FCSTD DOCUMENT  (FreeCAD 0.19R23578 (Git))
Label: z_axis_assembly
License: All rights reserved
LicenseURL: http://en.wikipedia.org/wiki/All_rights_reserved
objects: App::Link×12, App::DocumentObjectGroup×2, PartDesign::CoordinateSystem×2, App::FeaturePython×1, App::Part×1
note: 2 computed .brp shape members not serialized (recipe doc carries the construction recipe); baked Part::Feature solids carry a one-line shape summary decoded from their .brp
EXTERNAL_REF file=nut_block_t8_leadscrew.FCStd obj=LCS_1
EXTERNAL_REF file=nut_block_t8_leadscrew.FCStd obj=nut_block_t8_leadscrew
EXTERNAL_REF file=nut_block_standoff.FCStd obj=LCS_2
EXTERNAL_REF file=nut_block_t8_leadscrew.FCStd obj=LCS_0
EXTERNAL_REF file=nut_block_standoff.FCStd obj=Part018
EXTERNAL_REF file=nut_block_standoff.FCStd obj=LCS_1
EXTERNAL_REF file=z_axis_bearing_plate.FCStd obj=LCS_1
EXTERNAL_REF file=z_axis_bearing_plate.FCStd obj=Part017
EXTERNAL_REF file=SC12UU_bearing_block.FCStd obj=LCS_1
EXTERNAL_REF file=z_axis_bearing_plate.FCStd obj=LCS_2
EXTERNAL_REF file=SC12UU_bearing_block.FCStd obj=Part
EXTERNAL_REF file=z_axis_bearing_plate.FCStd obj=LCS_3
EXTERNAL_REF file=z_axis_bearing_plate.FCStd obj=LCS_4
EXTERNAL_REF file=z_axis_bearing_plate.FCStd obj=LCS_5
EXTERNAL_REF file=V-Slot 20x80x500 Linear Rail.FCStd obj=LCS_1
EXTERNAL_REF file=z_axis_bearing_plate.FCStd obj=LCS_6
EXTERNAL_REF file=V-Slot 20x80x500 Linear Rail.FCStd obj=Part
EXTERNAL_REF file=V-Slot 20x80x500 Linear Rail.FCStd obj=LCS_3
EXTERNAL_REF file=y_motor_bracket.FCStd obj=LCS_2
EXTERNAL_REF file=y_motor_bracket.FCStd obj=Part022
EXTERNAL_REF file=Nema 17  Stepper Motor length 60mm.FcStd obj=LCS_0
EXTERNAL_REF file=y_motor_bracket.FCStd obj=LCS_1
EXTERNAL_REF file=Nema 17  Stepper Motor length 60mm.FcStd obj=Part
EXTERNAL_REF file=Nema 17  Stepper Motor length 60mm.FcStd obj=LCS_1
EXTERNAL_REF file=2gt_pulley_20t.FCStd obj=LCS_1
EXTERNAL_REF file=2gt_pulley_20t.FCStd obj=Part
EXTERNAL_REF file=V-Slot 20x80x500 Linear Rail.FCStd obj=LCS_2
EXTERNAL_REF file=carriage_assembly.FCStd obj=LCS_1
EXTERNAL_REF file=carriage_assembly.FCStd obj=Model

FEATURE [App::DocumentObjectGroup] Parts
FEATURE [PartDesign::CoordinateSystem] LCS_Origin
  AttacherType = Attacher::AttachEngine3D
  MapMode = 2
  Support = -> [X_Axis]
FEATURE [App::DocumentObjectGroup] Constraints
FEATURE [App::FeaturePython] Variables  # WARN: FeaturePython — macro-defined, semantics opaque (R4)
FEATURE [App::Link] nut_block_t8_leadscrew_nut_block_t8_leadscrew
  AssemblyType = Asm4EE
  AttachedBy = #LCS_1
  AttachedTo = Parent Assembly#LCS_Origin
  AttachmentOffset = pos=(0,0,0) rot=(-1,0,0;4.71239rad)
  LinkPlacement = pos=(7.3e-15,5.3e-15,-10) rot=(0,0,1;4.71239rad)
  LinkedObject = -> <external nut_block_t8_leadscrew.FCStd>#nut_block_t8_leadscrew
  Placement = pos=(7.3e-15,5.3e-15,-10) rot=(0,0,1;4.71239rad)
  expr: Placement = LCS_Origin.Placement * AttachmentOffset * nut_block_t8_leadscrew#LCS_1.Placement ^ -1
FEATURE [App::Link] nut_block_standoff_nut_block_standoff
  AssemblyType = Asm4EE
  AttachedBy = #LCS_2
  AttachedTo = nut_block_t8_leadscrew_nut_block_t8_leadscrew#LCS_0
  AttachmentOffset = pos=(0,0,0) rot=(0,1,0;3.14159rad)
  LinkPlacement = pos=(28.4,6.44136e-07,6.5) rot=(-0.57735,-0.57735,0.57735;2.0944rad)
  LinkedObject = -> <external nut_block_standoff.FCStd>#Part018
  Placement = pos=(28.4,6.44136e-07,6.5) rot=(-0.57735,-0.57735,0.57735;2.0944rad)
  expr: Placement = nut_block_t8_leadscrew_nut_block_t8_leadscrew.Placement * nut_block_t8_leadscrew#LCS_0.Placement * AttachmentOffset * nut_block_standoff#LCS_2.Placement ^ -1
FEATURE [App::Link] z_axis_bearing_plate_bearing_plate
  AssemblyType = Asm4EE
  AttachedBy = #LCS_1
  AttachedTo = nut_block_standoff_nut_block_standoff#LCS_1
  AttachmentOffset = pos=(0,0,0) rot=(0,0,1;1.5708rad)
  LinkPlacement = pos=(28.4,6.44136e-07,6.5) rot=(0.57735,0.57735,0.57735;2.0944rad)
  LinkedObject = -> <external z_axis_bearing_plate.FCStd>#Part017
  Placement = pos=(28.4,6.44136e-07,6.5) rot=(0.57735,0.57735,0.57735;2.0944rad)
  expr: Placement = nut_block_standoff_nut_block_standoff.Placement * nut_block_standoff#LCS_1.Placement * AttachmentOffset * z_axis_bearing_plate#LCS_1.Placement ^ -1
FEATURE [App::Link] SC12UU_bearing_block_SC12UU_bearing_block
  AssemblyType = Asm4EE
  AttachedBy = #LCS_1
  AttachedTo = z_axis_bearing_plate_bearing_plate#LCS_2
  LinkPlacement = pos=(28.4,-95.25,-14.5) rot=(0,0,1;4.71239rad)
  LinkedObject = -> <external SC12UU_bearing_block.FCStd>#Part
  Placement = pos=(28.4,-95.25,-14.5) rot=(0,0,1;4.71239rad)
  expr: Placement = z_axis_bearing_plate_bearing_plate.Placement * z_axis_bearing_plate#LCS_2.Placement * AttachmentOffset * SC12UU_bearing_block#LCS_1.Placement ^ -1
FEATURE [App::Link] SC12UU_bearing_block_SC12UU_bearing_block_2
  AssemblyType = Asm4EE
  AttachedBy = #LCS_1
  AttachedTo = z_axis_bearing_plate_bearing_plate#LCS_3
  LinkPlacement = pos=(28.4,-95.25,27.5) rot=(0,0,1;4.71239rad)
  LinkedObject = -> <external SC12UU_bearing_block.FCStd>#Part
  Placement = pos=(28.4,-95.25,27.5) rot=(0,0,1;4.71239rad)
  expr: Placement = z_axis_bearing_plate_bearing_plate.Placement * z_axis_bearing_plate#LCS_3.Placement * AttachmentOffset * SC12UU_bearing_block#LCS_1.Placement ^ -1
FEATURE [App::Link] SC12UU_bearing_block_SC12UU_bearing_block_3
  AssemblyType = Asm4EE
  AttachedBy = #LCS_1
  AttachedTo = z_axis_bearing_plate_bearing_plate#LCS_4
  LinkPlacement = pos=(28.4,95.25,-14.5) rot=(0,0,1;4.71239rad)
  LinkedObject = -> <external SC12UU_bearing_block.FCStd>#Part
  Placement = pos=(28.4,95.25,-14.5) rot=(0,0,1;4.71239rad)
  expr: Placement = z_axis_bearing_plate_bearing_plate.Placement * z_axis_bearing_plate#LCS_4.Placement * AttachmentOffset * SC12UU_bearing_block#LCS_1.Placement ^ -1
FEATURE [App::Link] SC12UU_bearing_block_SC12UU_bearing_block_4
  AssemblyType = Asm4EE
  AttachedBy = #LCS_1
  AttachedTo = z_axis_bearing_plate_bearing_plate#LCS_5
  LinkPlacement = pos=(28.4,95.25,27.5) rot=(0,0,1;4.71239rad)
  LinkedObject = -> <external SC12UU_bearing_block.FCStd>#Part
  Placement = pos=(28.4,95.25,27.5) rot=(0,0,1;4.71239rad)
  expr: Placement = z_axis_bearing_plate_bearing_plate.Placement * z_axis_bearing_plate#LCS_5.Placement * AttachmentOffset * SC12UU_bearing_block#LCS_1.Placement ^ -1
FEATURE [App::Link] V_Slot_20x80x500_Linear_Rail_V_Slot_20x80x500_Linear_Rail  label="V_Slot_20x80x500_Linear_Rail_V-Slot 20x80x500 Linear Rail"
  AssemblyType = Asm4EE
  AttachedBy = #LCS_1
  AttachedTo = z_axis_bearing_plate_bearing_plate#LCS_6
  AttachmentOffset = pos=(0,0,0) rot=(0,0,1;1.5708rad)
  LinkPlacement = pos=(44.75,250,6.5) rot=(1,0,0;1.5708rad)
  LinkedObject = -> <external V-Slot 20x80x500 Linear Rail.FCStd>#Part
  Placement = pos=(44.75,250,6.5) rot=(1,0,0;1.5708rad)
  expr: Placement = z_axis_bearing_plate_bearing_plate.Placement * z_axis_bearing_plate#LCS_6.Placement * AttachmentOffset * V_Slot_20x80x500_Linear_Rail#LCS_1.Placement ^ -1
FEATURE [App::Link] y_motor_bracket_y_motor_bracket
  AssemblyType = Asm4EE
  AttachedBy = #LCS_2
  AttachedTo = V_Slot_20x80x500_Linear_Rail_V_Slot_20x80x500_Linear_Rail#LCS_3
  AttachmentOffset = pos=(0,0,0) rot=(0,0,1;4.71239rad)
  LinkPlacement = pos=(30.75,-252.5,18) rot=(0,0,1;0rad)
  LinkedObject = -> <external y_motor_bracket.FCStd>#Part022
  Placement = pos=(30.75,-252.5,18) rot=(0,0,1;0rad)
  expr: Placement = V_Slot_20x80x500_Linear_Rail_V_Slot_20x80x500_Linear_Rail.Placement * V_Slot_20x80x500_Linear_Rail#LCS_3.Placement * AttachmentOffset * y_motor_bracket#LCS_2.Placement ^ -1
FEATURE [App::Link] Nema_17__Stepper_Motor_length_60mm_Nema_17__Stepper_Motor_length_60mm  label="Nema_17__Stepper_Motor_length_60mm_Nema 17  Stepper Motor length 60mm"
  AssemblyType = Asm4EE
  AttachedBy = #LCS_0
  AttachedTo = y_motor_bracket_y_motor_bracket#LCS_1
  LinkPlacement = pos=(54.75,-274.5,81.4) rot=(-0.57735,0.57735,0.57735;4.18879rad)
  LinkedObject = -> <external Nema 17  Stepper Motor length 60mm.FcStd>#Part
  Placement = pos=(54.75,-274.5,81.4) rot=(-0.57735,0.57735,0.57735;4.18879rad)
  expr: Placement = y_motor_bracket_y_motor_bracket.Placement * y_motor_bracket#LCS_1.Placement * AttachmentOffset * Nema_17__Stepper_Motor_length_60mm#LCS_0.Placement ^ -1
FEATURE [App::Link] _gt_pulley_20t_2gt_pulley_20t
  AssemblyType = Asm4EE
  AttachedBy = #LCS_1
  AttachedTo = Nema_17__Stepper_Motor_length_60mm_Nema_17__Stepper_Motor_length_60mm#LCS_1
  AttachmentOffset = pos=(0,0,0) rot=(1,0,0;3.14159rad)
  LinkPlacement = pos=(54.75,-274.5,-2.2) rot=(0,-1,0;1.5708rad)
  LinkedObject = -> <external 2gt_pulley_20t.FCStd>#Part
  Placement = pos=(54.75,-274.5,-2.2) rot=(0,-1,0;1.5708rad)
  expr: Placement = Nema_17__Stepper_Motor_length_60mm_Nema_17__Stepper_Motor_length_60mm.Placement * Nema_17__Stepper_Motor_length_60mm#LCS_1.Placement * AttachmentOffset * _gt_pulley_20t#LCS_1.Placement ^ -1
FEATURE [App::Link] carriage_assembly
  AssemblyType = Asm4EE
  AttachedBy = #LCS_1
  AttachedTo = V_Slot_20x80x500_Linear_Rail_V_Slot_20x80x500_Linear_Rail#LCS_2
  LinkPlacement = pos=(56.25,1.2758e-06,6.5) rot=(0,0,1;0rad)
  LinkedObject = -> <external carriage_assembly.FCStd>#Model
  Placement = pos=(56.25,1.2758e-06,6.5) rot=(0,0,1;0rad)
  expr: Placement = V_Slot_20x80x500_Linear_Rail_V_Slot_20x80x500_Linear_Rail.Placement * V_Slot_20x80x500_Linear_Rail#LCS_2.Placement * AttachmentOffset * carriage_assembly#LCS_1.Placement ^ -1
FEATURE [PartDesign::CoordinateSystem] LCS_1
  AttacherType = Attacher::AttachEngine3D
  Placement = pos=(0,1e-15,2e-15) rot=(1,0,0;1.5708rad)
  expr: Placement = nut_block_t8_leadscrew_nut_block_t8_leadscrew.Placement * nut_block_t8_leadscrew#LCS_1.Placement * AttachmentOffset
FEATURE [App::Part] Model
  Configuration = 0
  Group = -> [LCS_Origin,Constraints,Variables,nut_block_t8_leadscrew_nut_block_t8_leadscrew,nut_block_standoff_nut_block_standoff,z_axis_bearing_plate_bearing_plate,SC12UU_bearing_block_SC12UU_bearing_block,SC12UU_bearing_block_SC12UU_bearing_block_2,SC12UU_bearing_block_SC12UU_bearing_block_3,SC12UU_bearing_block_SC12UU_bearing_block_4,V_Slot_20x80x500_Linear_Rail_V_Slot_20x80x500_Linear_Rail,+5 more]
  Origin = -> Origin
  Type = Assembly4 Model

RESOLVED EXTERNAL PARTS (link-assembly join: the EXTERNAL_REF files above that resolve inside this repo's crawl, each included once):
---- part carriage_assembly.FCStd = doc fcstd_ae16f4e09451 ----
FCSTD DOCUMENT  (FreeCAD 0.19R23578 (Git))
Label: carriage_assembly
License: All rights reserved
LicenseURL: http://en.wikipedia.org/wiki/All_rights_reserved
objects: App::Link×16, App::DocumentObjectGroup×2, PartDesign::CoordinateSystem×2, App::FeaturePython×1, App::Part×1
note: 2 computed .brp shape members not serialized (recipe doc carries the construction recipe); baked Part::Feature solids carry a one-line shape summary decoded from their .brp
EXTERNAL_REF file=y_axis_carriage_block.FCStd obj=Part026
EXTERNAL_REF file=x_axis_rail.FCStd obj=LCS_2
EXTERNAL_REF file=y_axis_carriage_block.FCStd obj=LCS_4
EXTERNAL_REF file=x_axis_rail.FCStd obj=Part028
EXTERNAL_REF file=x_axis_rail.FCStd obj=LCS_1
EXTERNAL_REF file=x_idler_bracket.FCStd obj=LCS_1
EXTERNAL_REF file=x_idler_bracket.FCStd obj=Part033
EXTERNAL_REF file=gates_2gt_idler_toothed.FCStd obj=LCS_1
EXTERNAL_REF file=x_idler_bracket.FCStd obj=LCS_2
EXTERNAL_REF file=gates_2gt_idler_toothed.FCStd obj=Part042
EXTERNAL_REF file=stock_motor_mount.FCStd obj=LCS_6
EXTERNAL_REF file=y_axis_carriage_block.FCStd obj=LCS_15
EXTERNAL_REF file=stock_motor_mount.FCStd obj=Part
EXTERNAL_REF file=Nema 17  Stepper Motor length 60mm.FcStd obj=LCS_0
EXTERNAL_REF file=stock_motor_mount.FCStd obj=LCS_1
EXTERNAL_REF file=Nema 17  Stepper Motor length 60mm.FcStd obj=Part
EXTERNAL_REF file=Nema 17  Stepper Motor length 60mm.FcStd obj=LCS_1
EXTERNAL_REF file=2gt_pulley_20t.FCStd obj=LCS_1
EXTERNAL_REF file=2gt_pulley_20t.FCStd obj=Part
EXTERNAL_REF file=watercooled_print_head.FCStd obj=LCS_1
EXTERNAL_REF file=x_axis_rail.FCStd obj=LCS_3
EXTERNAL_REF file=watercooled_print_head.FCStd obj=Model
EXTERNAL_REF file=Aluminum Spacer 6mm002.FCStd obj=LCS_1
EXTERNAL_REF file=y_axis_carriage_block.FCStd obj=LCS_12
EXTERNAL_REF file=Aluminum Spacer 6mm002.FCStd obj=Aluminum_Spacer_6mm002
EXTERNAL_REF file=y_axis_carriage_block.FCStd obj=LCS_11
EXTERNAL_REF file=eccentric_spacer.FCStd obj=LCS_1
EXTERNAL_REF file=y_axis_carriage_block.FCStd obj=LCS_13
EXTERNAL_REF file=eccentric_spacer.FCStd obj=Part
EXTERNAL_REF file=y_axis_carriage_block.FCStd obj=LCS_14
EXTERNAL_REF file=Aluminum Spacer 6mm002.FCStd obj=LCS_2
EXTERNAL_REF file=solid_v_wheel_assembly.FCStd obj=LCS_Origin
EXTERNAL_REF file=solid_v_wheel_assembly.FCStd obj=Model
EXTERNAL_REF file=eccentric_spacer.FCStd obj=LCS_2

FEATURE [App::DocumentObjectGroup] Parts
FEATURE [PartDesign::CoordinateSystem] LCS_Origin
  AttacherType = Attacher::AttachEngine3D
  MapMode = 2
  Support = -> [X_Axis]
FEATURE [App::DocumentObjectGroup] Constraints
FEATURE [App::FeaturePython] Variables  # WARN: FeaturePython — macro-defined, semantics opaque (R4)
FEATURE [App::Link] y_axis_carriage_block_y_axis_carriage_block001
  LinkedObject = -> <external y_axis_carriage_block.FCStd>#Part026
FEATURE [App::Link] x_axis_rail_2020_vslot_rail
  AssemblyType = Asm4EE
  AttachedBy = #LCS_2
  AttachedTo = y_axis_carriage_block_y_axis_carriage_block001#LCS_4
  AttachmentOffset = pos=(0,0,0) rot=(0,1,0;4.71239rad)
  LinkPlacement = pos=(57.675,-10,-1.34e-14) rot=(0.57735,-0.57735,0.57735;4.18879rad)
  LinkedObject = -> <external x_axis_rail.FCStd>#Part028
  Placement = pos=(57.675,-10,-1.34e-14) rot=(0.57735,-0.57735,0.57735;4.18879rad)
  expr: Placement = y_axis_carriage_block_y_axis_carriage_block001.Placement * y_axis_carriage_block#LCS_4.Placement * AttachmentOffset * x_axis_rail#LCS_2.Placement ^ -1
FEATURE [App::Link] x_idler_bracket_x_idler_bracket
  AssemblyType = Asm4EE
  AttachedBy = #LCS_1
  AttachedTo = x_axis_rail_2020_vslot_rail#LCS_1
  AttachmentOffset = pos=(0,0,0) rot=(0,0,1;4.71239rad)
  LinkPlacement = pos=(437.675,-10,-2.064e-13) rot=(0,0,1;0rad)
  LinkedObject = -> <external x_idler_bracket.FCStd>#Part033
  Placement = pos=(437.675,-10,-2.064e-13) rot=(0,0,1;0rad)
  expr: Placement = x_axis_rail_2020_vslot_rail.Placement * x_axis_rail#LCS_1.Placement * AttachmentOffset * x_idler_bracket#LCS_1.Placement ^ -1
FEATURE [App::Link] gates_2gt_idler_toothed_e3d_2gt_idler
  AssemblyType = Asm4EE
  AttachedBy = #LCS_1
  AttachedTo = x_idler_bracket_x_idler_bracket#LCS_2
  LinkPlacement = pos=(448.675,-24,-2.846e-13) rot=(-0.57735,-0.57735,-0.57735;2.0944rad)
  LinkedObject = -> <external gates_2gt_idler_toothed.FCStd>#Part042
  Placement = pos=(448.675,-24,-2.846e-13) rot=(-0.57735,-0.57735,-0.57735;2.0944rad)
  expr: Placement = x_idler_bracket_x_idler_bracket.Placement * x_idler_bracket#LCS_2.Placement * AttachmentOffset * gates_2gt_idler_toothed#LCS_1.Placement ^ -1
FEATURE [App::Link] stock_motor_mount_stock_motor_mount
  AssemblyType = Asm4EE
  AttachedBy = #LCS_6
  AttachedTo = y_axis_carriage_block_y_axis_carriage_block001#LCS_15
  LinkPlacement = pos=(9.35,-23,-36) rot=(0.57735,0.57735,0.57735;4.18879rad)
  LinkedObject = -> <external stock_motor_mount.FCStd>#Part
  Placement = pos=(9.35,-23,-36) rot=(0.57735,0.57735,0.57735;4.18879rad)
  expr: Placement = y_axis_carriage_block_y_axis_carriage_block001.Placement * y_axis_carriage_block#LCS_15.Placement * AttachmentOffset * stock_motor_mount#LCS_6.Placement ^ -1
FEATURE [App::Link] Nema_17__Stepper_Motor_length_60mm_Nema_17__Stepper_Motor_length_60mm  label="Nema_17__Stepper_Motor_length_60mm_Nema 17  Stepper Motor length 60mm"
  AssemblyType = Asm4EE
  AttachedBy = #LCS_0
  AttachedTo = stock_motor_mount_stock_motor_mount#LCS_1
  AttachmentOffset = pos=(0,0,0) rot=(1,0,0;3.14159rad)
  LinkPlacement = pos=(36.33,-23,73.42) rot=(0,0.707107,0.707107;3.14159rad)
  LinkedObject = -> <external Nema 17  Stepper Motor length 60mm.FcStd>#Part
  Placement = pos=(36.33,-23,73.42) rot=(0,0.707107,0.707107;3.14159rad)
  expr: Placement = stock_motor_mount_stock_motor_mount.Placement * stock_motor_mount#LCS_1.Placement * AttachmentOffset * Nema_17__Stepper_Motor_length_60mm#LCS_0.Placement ^ -1
FEATURE [App::Link] _gt_pulley_20t_2gt_pulley_20t
  AssemblyType = Asm4EE
  AttachedBy = #LCS_1
  AttachedTo = Nema_17__Stepper_Motor_length_60mm_Nema_17__Stepper_Motor_length_60mm#LCS_1
  AttachmentOffset = pos=(0,0,0) rot=(1,0,0;3.14159rad)
  LinkPlacement = pos=(36.33,-23,-10.18) rot=(-0.57735,-0.57735,-0.57735;2.0944rad)
  LinkedObject = -> <external 2gt_pulley_20t.FCStd>#Part
  Placement = pos=(36.33,-23,-10.18) rot=(-0.57735,-0.57735,-0.57735;2.0944rad)
  expr: Placement = Nema_17__Stepper_Motor_length_60mm_Nema_17__Stepper_Motor_length_60mm.Placement * Nema_17__Stepper_Motor_length_60mm#LCS_1.Placement * AttachmentOffset * _gt_pulley_20t#LCS_1.Placement ^ -1
FEATURE [App::Link] watercooled_print_head
  AssemblyType = Asm4EE
  AttachedBy = #LCS_1
  AttachedTo = x_axis_rail_2020_vslot_rail#LCS_3
  AttachmentOffset = pos=(0,0,0) rot=(0.57735,-0.57735,0.57735;2.0944rad)
  LinkPlacement = pos=(241.675,-40,-25) rot=(0,0,1;0rad)
  LinkedObject = -> <external watercooled_print_head.FCStd>#Model
  Placement = pos=(241.675,-40,-25) rot=(0,0,1;0rad)
  expr: Placement = x_axis_rail_2020_vslot_rail.Placement * x_axis_rail#LCS_3.Placement * AttachmentOffset * watercooled_print_head#LCS_1.Placement ^ -1
FEATURE [App::Link] Aluminum_Spacer_6mm002_Aluminum_Spacer_6mm002
  AssemblyType = Asm4EE
  AttachedBy = #LCS_1
  AttachedTo = y_axis_carriage_block_y_axis_carriage_block001#LCS_12
  LinkPlacement = pos=(-6,40,49.85) rot=(0,-1,0;4.71239rad)
  LinkedObject = -> <external Aluminum Spacer 6mm002.FCStd>#Aluminum_Spacer_6mm002
  Placement = pos=(-6,40,49.85) rot=(0,-1,0;4.71239rad)
  expr: Placement = y_axis_carriage_block_y_axis_carriage_block001.Placement * y_axis_carriage_block#LCS_12.Placement * AttachmentOffset * Aluminum_Spacer_6mm002#LCS_1.Placement ^ -1
FEATURE [App::Link] Aluminum_Spacer_6mm002_Aluminum_Spacer_6mm003
  AssemblyType = Asm4EE
  AttachedBy = #LCS_1
  AttachedTo = y_axis_carriage_block_y_axis_carriage_block001#LCS_11
  LinkPlacement = pos=(-6,-40,49.85) rot=(0,-1,0;4.71239rad)
  LinkedObject = -> <external Aluminum Spacer 6mm002.FCStd>#Aluminum_Spacer_6mm002
  Placement = pos=(-6,-40,49.85) rot=(0,-1,0;4.71239rad)
  expr: Placement = y_axis_carriage_block_y_axis_carriage_block001.Placement * y_axis_carriage_block#LCS_11.Placement * AttachmentOffset * Aluminum_Spacer_6mm002#LCS_1.Placement ^ -1
FEATURE [App::Link] eccentric_spacer_eccentric_spacer
  AssemblyType = Asm4EE
  AttachedBy = #LCS_1
  AttachedTo = y_axis_carriage_block_y_axis_carriage_block001#LCS_13
  AttachmentOffset = pos=(0,0,0) rot=(1,0,0;3.14159rad)
  LinkPlacement = pos=(0,40,-49.85) rot=(-0.707107,0,0.707107;3.14159rad)
  LinkedObject = -> <external eccentric_spacer.FCStd>#Part
  Placement = pos=(0,40,-49.85) rot=(-0.707107,0,0.707107;3.14159rad)
  expr: Placement = y_axis_carriage_block_y_axis_carriage_block001.Placement * y_axis_carriage_block#LCS_13.Placement * AttachmentOffset * eccentric_spacer#LCS_1.Placement ^ -1
FEATURE [App::Link] eccentric_spacer_eccentric_spacer_2
  AssemblyType = Asm4EE
  AttachedBy = #LCS_1
  AttachedTo = y_axis_carriage_block_y_axis_carriage_block001#LCS_14
  AttachmentOffset = pos=(0,0,0) rot=(0,-1,0;3.14159rad)
  LinkPlacement = pos=(0,-40,-49.85) rot=(0,-1,0;1.5708rad)
  LinkedObject = -> <external eccentric_spacer.FCStd>#Part
  Placement = pos=(0,-40,-49.85) rot=(0,-1,0;1.5708rad)
  expr: Placement = y_axis_carriage_block_y_axis_carriage_block001.Placement * y_axis_carriage_block#LCS_14.Placement * AttachmentOffset * eccentric_spacer#LCS_1.Placement ^ -1
FEATURE [App::Link] solid_v_wheel_assembly
  AssemblyType = Asm4EE
  AttachedBy = #LCS_Origin
  AttachedTo = Aluminum_Spacer_6mm002_Aluminum_Spacer_6mm002#LCS_2
  LinkPlacement = pos=(-6,40,49.85) rot=(0.57735,-0.57735,0.57735;4.18879rad)
  LinkedObject = -> <external solid_v_wheel_assembly.FCStd>#Model
  Placement = pos=(-6,40,49.85) rot=(0.57735,-0.57735,0.57735;4.18879rad)
  expr: Placement = Aluminum_Spacer_6mm002_Aluminum_Spacer_6mm002.Placement * Aluminum_Spacer_6mm002#LCS_2.Placement * AttachmentOffset * solid_v_wheel_assembly#LCS_Origin.Placement ^ -1
FEATURE [App::Link] solid_v_wheel_assembly_2
  AssemblyType = Asm4EE
  AttachedBy = #LCS_Origin
  AttachedTo = Aluminum_Spacer_6mm002_Aluminum_Spacer_6mm003#LCS_2
  LinkPlacement = pos=(-6,-40,49.85) rot=(0.57735,-0.57735,0.57735;4.18879rad)
  LinkedObject = -> <external solid_v_wheel_assembly.FCStd>#Model
  Placement = pos=(-6,-40,49.85) rot=(0.57735,-0.57735,0.57735;4.18879rad)
  expr: Placement = Aluminum_Spacer_6mm002_Aluminum_Spacer_6mm003.Placement * Aluminum_Spacer_6mm002#LCS_2.Placement * AttachmentOffset * solid_v_wheel_assembly#LCS_Origin.Placement ^ -1
FEATURE [App::Link] solid_v_wheel_assembly_3
  AssemblyType = Asm4EE
  AttachedBy = #LCS_Origin
  AttachedTo = eccentric_spacer_eccentric_spacer#LCS_2
  AttachmentOffset = pos=(0,0,0) rot=(0,-1,0;3.14159rad)
  LinkPlacement = pos=(-6,40.78,-49.85) rot=(0.57735,0.57735,0.57735;2.0944rad)
  LinkedObject = -> <external solid_v_wheel_assembly.FCStd>#Model
  Placement = pos=(-6,40.78,-49.85) rot=(0.57735,0.57735,0.57735;2.0944rad)
  expr: Placement = eccentric_spacer_eccentric_spacer.Placement * eccentric_spacer#LCS_2.Placement * AttachmentOffset * solid_v_wheel_assembly#LCS_Origin.Placement ^ -1
FEATURE [App::Link] solid_v_wheel_assembly_4
  AssemblyType = Asm4EE
  AttachedBy = #LCS_Origin
  AttachedTo = eccentric_spacer_eccentric_spacer_2#LCS_2
  AttachmentOffset = pos=(0,0,0) rot=(0,1,0;3.14159rad)
  LinkPlacement = pos=(-6,-40.78,-49.85) rot=(-0.57735,0.57735,-0.57735;2.0944rad)
  LinkedObject = -> <external solid_v_wheel_assembly.FCStd>#Model
  Placement = pos=(-6,-40.78,-49.85) rot=(-0.57735,0.57735,-0.57735;2.0944rad)
  expr: Placement = eccentric_spacer_eccentric_spacer_2.Placement * eccentric_spacer#LCS_2.Placement * AttachmentOffset * solid_v_wheel_assembly#LCS_Origin.Placement ^ -1
FEATURE [PartDesign::CoordinateSystem] LCS_1
  AttacherType = Attacher::AttachEngine3D
  AttachmentOffset = pos=(-11.5,0,0) rot=(0,0,1;0rad)
  MapMode = 2
  Placement = pos=(-11.5,0,0) rot=(0,0,1;0rad)
  Support = -> [LCS_Origin]
FEATURE [App::Part] Model
  Configuration = 0
  Group = -> [LCS_Origin,Constraints,Variables,y_axis_carriage_block_y_axis_carriage_block001,x_axis_rail_2020_vslot_rail,x_idler_bracket_x_idler_bracket,gates_2gt_idler_toothed_e3d_2gt_idler,stock_motor_mount_stock_motor_mount,Nema_17__Stepper_Motor_length_60mm_Nema_17__Stepper_Motor_length_60mm,_gt_pulley_20t_2gt_pulley_20t,watercooled_print_head,Aluminum_Spacer_6mm002_Aluminum_Spacer_6mm002,+8 more]
  Origin = -> Origin
  Type = Assembly4 Model
---- part nut_block_standoff.FCStd = doc fcstd_659b3a1c4ef2 ----
FCSTD DOCUMENT  (FreeCAD 0.19R23578 (Git))
Label: nut_block_standoff
License: All rights reserved
LicenseURL: http://en.wikipedia.org/wiki/All_rights_reserved
objects: Sketcher::SketchObject×3, PartDesign::Hole×2, PartDesign::CoordinateSystem×2, PartDesign::Pad×1, PartDesign::Body×1, App::Part×1
note: 12 computed .brp shape members not serialized (recipe doc carries the construction recipe); baked Part::Feature solids carry a one-line shape summary decoded from their .brp

FEATURE [Sketcher::SketchObject] Sketch026
  MapMode = 5
  Placement = pos=(0,0,0) rot=(0.57735,0.57735,0.57735;2.0944rad)
  Support = -> [YZ_Plane030]
  sketch-geometry (10):
    g0: LineSegment StartX=-30 StartY=0 StartZ=0 EndX=-30 EndY=2 EndZ=0
    g1: LineSegment StartX=-30 StartY=2 StartZ=0 EndX=-16.5 EndY=22.4 EndZ=0
    g2: LineSegment StartX=-16.5 StartY=22.4 StartZ=0 EndX=16.5 EndY=22.4 EndZ=0
    g3: LineSegment StartX=16.5 StartY=22.4 StartZ=0 EndX=30 EndY=2 EndZ=0
    g4: LineSegment StartX=30 StartY=2 StartZ=0 EndX=30 EndY=0 EndZ=0
    g5: LineSegment StartX=30 StartY=0 StartZ=0 EndX=-30 EndY=0 EndZ=0
    g6: ArcOfCircle CenterX=-11 CenterY=11.2 CenterZ=0 NormalX=0 NormalY=0 NormalZ=1 AngleXU=0 Radius=6.5 StartAngle=1.5708 EndAngle=4.71239
    g7: ArcOfCircle CenterX=11 CenterY=11.2 CenterZ=0 NormalX=0 NormalY=0 NormalZ=1 AngleXU=0 Radius=6.5 StartAngle=4.71239 EndAngle=7.85398
    g8: LineSegment StartX=-11 StartY=4.7 StartZ=0 EndX=11 EndY=4.7 EndZ=0
    g9: LineSegment StartX=-11 StartY=17.7 StartZ=0 EndX=11 EndY=17.7 EndZ=0
  constraints (25):
    c: Coincident(g0,g5)
    c: Coincident(g0,g1)
    c: Coincident(g1,g2)
    c: Coincident(g2,g3)
    c: Coincident(g3,g4)
    c: Coincident(g4,g5)
    c: Vertical(g0)
    c: Vertical(g4)
    c: PointOnObject(g-1,g5)
    c: DistanceX(g5,g5) = 60
    c: DistanceX(g2,g2) = 33
    c: DistanceY(g0,g0) = 2
    c: Equal(g0,g4)
    c: DistanceY(g4,g2) = 22.4
    c: Symmetric(g1,g2,g-2)
    c: Symmetric(g0,g4,g-2)
    c: Tangent(g6,g9) = 1.5708
    c: Tangent(g6,g8) = -1.5708
    c: Tangent(g8,g7) = -1.5708
    c: Tangent(g9,g7) = 1.5708
    c: Horizontal(g8)
    c: Symmetric(g6,g7,g-2)
    c: Distance(g6,g6) = 13
    c: DistanceY(g-1,g6) = 11.2
    c: DistanceX(g6,g7) = 22
FEATURE [PartDesign::Pad] Pad002
  AllowMultiFace = false
  Direction = (1,1,1)
  Length = 34
  Length2 = 100
  Midplane = true
  Placement = pos=(0,0,0) rot=(0.57735,0.57735,0.57735;2.0944rad)
  Profile = -> Sketch026
  Type = 0
FEATURE [Sketcher::SketchObject] Sketch027
  MapMode = 5
  Placement = pos=(0,0,0) rot=(0,1,0;3.14159rad)
  Support = -> [XY_Plane030]
  sketch-geometry (11):
    g0: Circle CenterX=-10 CenterY=24 CenterZ=0 NormalX=0 NormalY=0 NormalZ=1 AngleXU=0 Radius=2.5
    g1: Circle CenterX=-10 CenterY=-24 CenterZ=0 NormalX=0 NormalY=0 NormalZ=1 AngleXU=0 Radius=2.5
    g2: Circle CenterX=10 CenterY=-24 CenterZ=0 NormalX=0 NormalY=0 NormalZ=1 AngleXU=0 Radius=2.5
    g3: Circle CenterX=10 CenterY=24 CenterZ=0 NormalX=0 NormalY=0 NormalZ=1 AngleXU=0 Radius=2.5
    g4: LineSegment StartX=-10 StartY=24 StartZ=0 EndX=10 EndY=24 EndZ=0
    g5: LineSegment StartX=10 StartY=24 StartZ=0 EndX=10 EndY=-24 EndZ=0
    g6: LineSegment StartX=10 StartY=-24 StartZ=0 EndX=-10 EndY=-24 EndZ=0
    g7: LineSegment StartX=-10 StartY=-24 StartZ=0 EndX=-10 EndY=24 EndZ=0
    g8: LineSegment StartX=-10 StartY=24 StartZ=0 EndX=10 EndY=-24 EndZ=0
    g9: LineSegment StartX=-10 StartY=-24 StartZ=0 EndX=10 EndY=24 EndZ=0
    g10: GeomPoint X=0 Y=0 Z=0
  constraints (25):
    c: Coincident(g4,g5)
    c: Coincident(g5,g6)
    c: Coincident(g6,g7)
    c: Coincident(g7,g4)
    c: Horizontal(g4)
    c: Horizontal(g6)
    c: Vertical(g5)
    c: Vertical(g7)
    c: Coincident(g4,g0)
    c: Coincident(g5,g2)
    c: Coincident(g3,g4)
    c: Coincident(g1,g6)
    c: Diameter(g0) = 5
    c: Equal(g0,g3)
    c: Equal(g3,g1)
    c: Equal(g1,g2)
    c: Coincident(g8,g2)
    c: Coincident(g9,g1)
    c: Coincident(g9,g3)
    c: PointOnObject(g10,g8)
    c: PointOnObject(g10,g9)
    c: Coincident(g10,g-1)
    c: DistanceX(g6,g6) = 20
    c: Coincident(g8,g0)
    c: DistanceY(g5,g5) = 48
FEATURE [PartDesign::Hole] Hole002
  AllowMultiFace = false
  BaseFeature = -> Pad002
  Depth = 25
  DepthType = 1
  Diameter = 1.6
  DrillPoint = 0
  DrillPointAngle = 118
  HoleCutCountersinkAngle = 90
  HoleCutDepth = 0
  HoleCutDiameter = 5
  HoleCutType = 0
  ModelActualThread = false
  Placement = pos=(0,0,0) rot=(0.57735,0.57735,0.57735;2.0944rad)
  Profile = -> Sketch027
  Tapered = false
  TaperedAngle = 90
  ThreadAngle = 60
  ThreadClass = 0
  ThreadCutOffInner = 0.0433013
  ThreadCutOffOuter = 0.0866025
  ThreadDirection = 1
  ThreadFit = 0
  ThreadPitch = 0.4
  ThreadSize = 6
  ThreadType = 1
  Threaded = true
FEATURE [Sketcher::SketchObject] Sketch028
  AttachmentOffset = pos=(0,0,22.4) rot=(0,0,1;0rad)
  MapMode = 5
  Placement = pos=(0,0,22.4) rot=(0,0,1;0rad)
  Support = -> [XY_Plane030]
  sketch-geometry (2):
    g0: Circle CenterX=-10 CenterY=6.5 CenterZ=0 NormalX=0 NormalY=0 NormalZ=1 AngleXU=0 Radius=2.5
    g1: Circle CenterX=10 CenterY=6.5 CenterZ=0 NormalX=0 NormalY=0 NormalZ=1 AngleXU=0 Radius=2.5
  constraints (5):
    c: Symmetric(g0,g1,g-2)
    c: Diameter(g0) = 5
    c: Equal(g0,g1)
    c: DistanceX(g0,g-1) = 10
    c: DistanceY(g-1,g0) = 6.5
FEATURE [PartDesign::Hole] Hole001
  AllowMultiFace = false
  BaseFeature = -> Hole002
  Depth = 5
  DepthType = 0
  Diameter = 1.6
  DrillPoint = 0
  DrillPointAngle = 118
  HoleCutCountersinkAngle = 90
  HoleCutDepth = 0
  HoleCutDiameter = 5
  HoleCutType = 0
  ModelActualThread = false
  Placement = pos=(0,0,0) rot=(0.57735,0.57735,0.57735;2.0944rad)
  Profile = -> Sketch028
  Tapered = false
  TaperedAngle = 90
  ThreadAngle = 60
  ThreadClass = 0
  ThreadCutOffInner = 0.0433013
  ThreadCutOffOuter = 0.0866025
  ThreadDirection = 1
  ThreadFit = 0
  ThreadPitch = 0.4
  ThreadSize = 6
  ThreadType = 1
  Threaded = true
FEATURE [PartDesign::Body] Body011  label="Body"
  Group = -> [Sketch026,Pad002,Sketch027,Hole002,Sketch028,Hole001]
  Origin = -> Origin030
  Tip = -> Hole001
FEATURE [PartDesign::CoordinateSystem] LCS_1
  AttacherType = Attacher::AttachEngine3D
  MapMode = 5
  Placement = pos=(0,0,-1e-16) rot=(0.707107,0.707107,0;3.14159rad)
  Support = -> [Hole001]
FEATURE [PartDesign::CoordinateSystem] LCS_2
  AttacherType = Attacher::AttachEngine3D
  MapMode = 45
  Placement = pos=(-5.4e-15,6.5,22.4) rot=(0,0,1;1.5708rad)
  Support = -> [Hole001]
FEATURE [App::Part] Part018  label="nut_block_standoff"
  Group = -> [Body011,LCS_1,LCS_2]
  Origin = -> Origin025
---- part y_motor_bracket.FCStd = doc fcstd_277c75dd18b4 ----
FCSTD DOCUMENT  (FreeCAD 0.19R23578 (Git))
Label: y_motor_bracket
License: All rights reserved
LicenseURL: http://en.wikipedia.org/wiki/All_rights_reserved
objects: Sketcher::SketchObject×4, PartDesign::Pad×3, PartDesign::CoordinateSystem×2, PartDesign::Pocket×1, PartDesign::Body×1, App::Part×1
note: 15 computed .brp shape members not serialized (recipe doc carries the construction recipe); baked Part::Feature solids carry a one-line shape summary decoded from their .brp

FEATURE [Sketcher::SketchObject] Sketch029
  MapMode = 5
  Placement = pos=(0,0,0) rot=(0.57735,0.57735,0.57735;2.0944rad)
  Support = -> [YZ_Plane035]
  sketch-geometry (10):
    g0: LineSegment StartX=0 StartY=4 StartZ=0 EndX=25 EndY=4 EndZ=0
    g1: LineSegment StartX=25 StartY=4 StartZ=0 EndX=25 EndY=-51 EndZ=0
    g2: LineSegment StartX=25 StartY=-51 StartZ=0 EndX=0 EndY=-51 EndZ=0
    g3: ArcOfCircle CenterX=12.5 CenterY=-5 CenterZ=0 NormalX=0 NormalY=0 NormalZ=1 AngleXU=0 Radius=2.55 StartAngle=2.224e-13 EndAngle=3.14159
    g4: ArcOfCircle CenterX=12.5 CenterY=-42 CenterZ=0 NormalX=0 NormalY=0 NormalZ=1 AngleXU=0 Radius=2.55 StartAngle=3.14159 EndAngle=6.28319
    g5: LineSegment StartX=9.95 StartY=-5 StartZ=0 EndX=9.95 EndY=-42 EndZ=0
    g6: LineSegment StartX=15.05 StartY=-5 StartZ=0 EndX=15.05 EndY=-42 EndZ=0
    g7: LineSegment StartX=0 StartY=-51 StartZ=0 EndX=-44 EndY=0 EndZ=0
    g8: LineSegment StartX=-44 StartY=0 StartZ=0 EndX=0 EndY=0 EndZ=0
    g9: LineSegment StartX=0 StartY=4 StartZ=0 EndX=0 EndY=0 EndZ=0
  constraints (27):
    c: Horizontal(g0)
    c: Horizontal(g2)
    c: Vertical(g1)
    c: Tangent(g3,g6) = 1.5708
    c: Tangent(g3,g5) = -1.5708
    c: Tangent(g5,g4) = -1.5708
    c: Tangent(g6,g4) = 1.5708
    c: Vertical(g5)
    c: Equal(g3,g4)
    c: DistanceX(g0,g4) = 12.5
    c: Diameter(g3) = 5.1
    c: DistanceY(g4,g0) = 46
    c: Coincident(g0,g1)
    c: DistanceX(g2,g2) = 25
    c: Coincident(g2,g1)
    c: PointOnObject(g0,g-2)
    c: DistanceY(g-1,g0) = 4
    c: DistanceY(g3,g-1) = 5
    c: DistanceY(g2,g-1) = 51
    c: Coincident(g7,g2)
    c: PointOnObject(g7,g-1)
    c: Coincident(g8,g7)
    c: Coincident(g8,g-1)
    c: Coincident(g9,g0)
    c: Coincident(g9,g8)
    c: DistanceX(g7,g8) = 44
    c: PointOnObject(g2,g-2)
FEATURE [PartDesign::Pad] Pad012
  AllowMultiFace = false
  Direction = (1,1,1)
  Length = 4
  Length2 = 100
  Placement = pos=(0,0,0) rot=(0.57735,0.57735,0.57735;2.0944rad)
  Profile = -> Sketch029
  Type = 0
FEATURE [Sketcher::SketchObject] Sketch030
  MapMode = 5
  Placement = pos=(0,0,0) rot=(0.57735,0.57735,0.57735;2.0944rad)
  Support = -> [YZ_Plane035]
  sketch-geometry (4):
    g0: LineSegment StartX=0 StartY=0 StartZ=0 EndX=-44 EndY=0 EndZ=0
    g1: LineSegment StartX=-44 StartY=0 StartZ=0 EndX=-44 EndY=4 EndZ=0
    g2: LineSegment StartX=-44 StartY=4 StartZ=0 EndX=0 EndY=4 EndZ=0
    g3: LineSegment StartX=0 StartY=4 StartZ=0 EndX=0 EndY=0 EndZ=0
  constraints (11):
    c: Coincident(g0,g1)
    c: Coincident(g1,g2)
    c: Coincident(g2,g3)
    c: Coincident(g3,g0)
    c: Horizontal(g0)
    c: Horizontal(g2)
    c: Vertical(g1)
    c: Vertical(g3)
    c: Coincident(g0,g-1)
    c: DistanceY(g1,g1) = 4
    c: DistanceX(g0,g0) = 44
FEATURE [PartDesign::Pad] Pad013
  AllowMultiFace = false
  BaseFeature = -> Pad012
  Direction = (1,1,1)
  Length = 46
  Length2 = 100
  Placement = pos=(0,0,0) rot=(0.57735,0.57735,0.57735;2.0944rad)
  Profile = -> Sketch030
  Type = 0
FEATURE [Sketcher::SketchObject] Sketch031
  MapMode = 5
  Support = -> [XY_Plane035]
  sketch-geometry (11):
    g0: Circle CenterX=8.5 CenterY=-6.5 CenterZ=0 NormalX=0 NormalY=0 NormalZ=1 AngleXU=0 Radius=1.55
    g1: Circle CenterX=39.5 CenterY=-6.5 CenterZ=0 NormalX=0 NormalY=0 NormalZ=1 AngleXU=0 Radius=1.55
    g2: Circle CenterX=39.5 CenterY=-37.5 CenterZ=0 NormalX=0 NormalY=0 NormalZ=1 AngleXU=0 Radius=1.55
    g3: Circle CenterX=8.5 CenterY=-37.5 CenterZ=0 NormalX=0 NormalY=0 NormalZ=1 AngleXU=0 Radius=1.55
    g4: Circle CenterX=24 CenterY=-22 CenterZ=0 NormalX=0 NormalY=0 NormalZ=1 AngleXU=0 Radius=11
    g5: LineSegment StartX=8.5 StartY=-6.5 StartZ=0 EndX=39.5 EndY=-6.5 EndZ=0
    g6: LineSegment StartX=39.5 StartY=-6.5 StartZ=0 EndX=39.5 EndY=-37.5 EndZ=0
    g7: LineSegment StartX=39.5 StartY=-37.5 StartZ=0 EndX=8.5 EndY=-37.5 EndZ=0
    g8: LineSegment StartX=8.5 StartY=-37.5 StartZ=0 EndX=8.5 EndY=-6.5 EndZ=0
    g9: LineSegment StartX=8.5 StartY=-6.5 StartZ=0 EndX=39.5 EndY=-37.5 EndZ=0
    g10: LineSegment StartX=39.5 StartY=-6.5 StartZ=0 EndX=8.5 EndY=-37.5 EndZ=0
  constraints (27):
    c: Coincident(g5,g6)
    c: Coincident(g6,g7)
    c: Coincident(g7,g8)
    c: Coincident(g8,g5)
    c: Horizontal(g5)
    c: Horizontal(g7)
    c: Vertical(g6)
    c: Vertical(g8)
    c: Coincident(g5,g0)
    c: Coincident(g6,g2)
    c: Coincident(g3,g7)
    c: Coincident(g1,g5)
    c: DistanceY(g6,g6) = 31
    c: DistanceX(g5,g5) = 31
    c: DistanceX(g-1,g0) = 8.5
    c: DistanceY(g0,g-1) = 6.5
    c: Coincident(g9,g0)
    c: Coincident(g9,g2)
    c: Coincident(g10,g1)
    c: Coincident(g10,g3)
    c: PointOnObject(g4,g10)
    c: PointOnObject(g4,g9)
    c: Equal(g0,g1)
    c: Equal(g1,g2)
    c: Equal(g2,g3)
    c: Diameter(g1) = 3.1
    c: Diameter(g4) = 22
FEATURE [PartDesign::Pocket] Pocket012
  AllowMultiFace = false
  BaseFeature = -> Pad013
  Length = 5
  Length2 = 100
  Placement = pos=(0,0,0) rot=(0.57735,0.57735,0.57735;2.0944rad)
  Profile = -> Sketch031
  Reversed = true
  Type = 1
FEATURE [Sketcher::SketchObject] Sketch032
  MapMode = 5
  Placement = pos=(0,0,0) rot=(-0.57735,0.57735,0.57735;4.18879rad)
  Support = -> [YZ_Plane035]
  sketch-geometry (4):
    g0: LineSegment StartX=21 StartY=4 StartZ=0 EndX=25 EndY=4 EndZ=0
    g1: LineSegment StartX=25 StartY=4 StartZ=0 EndX=25 EndY=-21 EndZ=0
    g2: LineSegment StartX=25 StartY=-21 StartZ=0 EndX=21 EndY=-21 EndZ=0
    g3: LineSegment StartX=21 StartY=-21 StartZ=0 EndX=21 EndY=4 EndZ=0
  constraints (12):
    c: Coincident(g0,g1)
    c: Coincident(g1,g2)
    c: Coincident(g2,g3)
    c: Coincident(g3,g0)
    c: Horizontal(g0)
    c: Horizontal(g2)
    c: Vertical(g1)
    c: Vertical(g3)
    c: DistanceY(g1,g1) = 25
    c: DistanceX(g0,g0) = 4
    c: DistanceY(g-1,g0) = 4
    c: DistanceX(g-1,g0) = 21
FEATURE [PartDesign::Pad] Pad003
  AllowMultiFace = false
  BaseFeature = -> Pocket012
  Direction = (1,1,1)
  Length = 45
  Length2 = 100
  Placement = pos=(0,0,0) rot=(0.57735,0.57735,0.57735;2.0944rad)
  Profile = -> Sketch032
  Type = 0
FEATURE [PartDesign::Body] Body012
  Group = -> [Sketch029,Pad012,Sketch030,Pad013,Sketch031,Pocket012,Sketch032,Pad003]
  Origin = -> Origin035
  Tip = -> Pad003
FEATURE [PartDesign::CoordinateSystem] LCS_1
  AttacherType = Attacher::AttachEngine3D
  MapMode = 11
  Placement = pos=(24,-22,4) rot=(-0.707107,0.707107,0;3.14159rad)
  Support = -> [Pad003]
FEATURE [PartDesign::CoordinateSystem] LCS_2
  AttacherType = Attacher::AttachEngine3D
  MapMode = 45
  Placement = pos=(4,12.5,-23.5) rot=(0.57735,0.57735,0.57735;2.0944rad)
  Support = -> [Pad003]
FEATURE [App::Part] Part022  label="y_motor_bracket"
  Group = -> [Body012,LCS_1,LCS_2]
  Origin = -> Origin032
---- part z_axis_bearing_plate.FCStd = doc fcstd_f6f6e68a77d2 ----
FCSTD DOCUMENT  (FreeCAD 0.19R23578 (Git))
Label: z_axis_bearing_plate
License: All rights reserved
LicenseURL: http://en.wikipedia.org/wiki/All_rights_reserved
objects: PartDesign::CoordinateSystem×6, Sketcher::SketchObject×3, PartDesign::Pad×1, PartDesign::Hole×1, PartDesign::Pocket×1, PartDesign::Body×1, App::Part×1
note: 16 computed .brp shape members not serialized (recipe doc carries the construction recipe); baked Part::Feature solids carry a one-line shape summary decoded from their .brp

FEATURE [Sketcher::SketchObject] Sketch023
  MapMode = 5
  Support = -> [XY_Plane029]
  sketch-geometry (6):
    g0: LineSegment StartX=-116.25 StartY=40 StartZ=0 EndX=116.25 EndY=40 EndZ=0
    g1: LineSegment StartX=116.25 StartY=40 StartZ=0 EndX=116.25 EndY=-40 EndZ=0
    g2: LineSegment StartX=116.25 StartY=-40 StartZ=0 EndX=-116.25 EndY=-40 EndZ=0
    g3: LineSegment StartX=-116.25 StartY=-40 StartZ=0 EndX=-116.25 EndY=40 EndZ=0
    g4: LineSegment StartX=-116.25 StartY=40 StartZ=0 EndX=116.25 EndY=-40 EndZ=0
    g5: LineSegment StartX=116.25 StartY=40 StartZ=0 EndX=-116.25 EndY=-40 EndZ=0
  constraints (16):
    c: Coincident(g0,g1)
    c: Coincident(g1,g2)
    c: Coincident(g2,g3)
    c: Coincident(g3,g0)
    c: Horizontal(g0)
    c: Horizontal(g2)
    c: Vertical(g1)
    c: Vertical(g3)
    c: DistanceX(g0,g0) = 232.5  'plate_width'
    c: DistanceY(g3,g3) = 80  'plate_height'
    c: Coincident(g4,g0)
    c: Coincident(g4,g1)
    c: Coincident(g5,g0)
    c: Coincident(g5,g2)
    c: PointOnObject(g-1,g5)
    c: PointOnObject(g-1,g4)
FEATURE [PartDesign::Pad] Pad011
  AllowMultiFace = false
  Direction = (1,1,1)
  Length = 6.35
  Length2 = 100
  Profile = -> Sketch023
  Type = 0
FEATURE [Sketcher::SketchObject] Sketch024
  AttachmentOffset = pos=(0,0,6.35) rot=(0,0,1;0rad)
  MapMode = 5
  Placement = pos=(0,0,6.35) rot=(0,0,1;0rad)
  Support = -> [XY_Plane029]
  sketch-geometry (55):
    g0: Circle CenterX=-110.5 CenterY=34 CenterZ=0 NormalX=0 NormalY=0 NormalZ=1 AngleXU=0 Radius=2.55
    g1: Circle CenterX=-110.5 CenterY=8 CenterZ=0 NormalX=0 NormalY=0 NormalZ=1 AngleXU=0 Radius=2.55
    g2: Circle CenterX=-80 CenterY=34 CenterZ=0 NormalX=0 NormalY=0 NormalZ=1 AngleXU=0 Radius=2.55
    g3: Circle CenterX=-80 CenterY=8 CenterZ=0 NormalX=0 NormalY=0 NormalZ=1 AngleXU=0 Radius=2.55
    g4: LineSegment StartX=-110.5 StartY=34 StartZ=0 EndX=-80 EndY=34 EndZ=0
    g5: LineSegment StartX=-80 StartY=34 StartZ=0 EndX=-80 EndY=8 EndZ=0
    g6: LineSegment StartX=-80 StartY=8 StartZ=0 EndX=-110.5 EndY=8 EndZ=0
    g7: LineSegment StartX=-110.5 StartY=8 StartZ=0 EndX=-110.5 EndY=34 EndZ=0
    g8: GeomPoint X=-95.25 Y=21 Z=0
    g9: LineSegment StartX=-110.5 StartY=34 StartZ=0 EndX=-80 EndY=8 EndZ=0
    g10: LineSegment StartX=-80 StartY=34 StartZ=0 EndX=-110.5 EndY=8 EndZ=0
    g11: Circle CenterX=80 CenterY=34 CenterZ=0 NormalX=0 NormalY=0 NormalZ=1 AngleXU=0 Radius=2.55
    g12: Circle CenterX=80 CenterY=8 CenterZ=0 NormalX=0 NormalY=0 NormalZ=1 AngleXU=0 Radius=2.55
    g13: Circle CenterX=110.5 CenterY=34 CenterZ=0 NormalX=0 NormalY=0 NormalZ=1 AngleXU=0 Radius=2.55
    g14: Circle CenterX=110.5 CenterY=8 CenterZ=0 NormalX=0 NormalY=0 NormalZ=1 AngleXU=0 Radius=2.55
    g15: LineSegment StartX=80 StartY=34 StartZ=0 EndX=110.5 EndY=34 EndZ=0
    g16: LineSegment StartX=110.5 StartY=34 StartZ=0 EndX=110.5 EndY=8 EndZ=0
    g17: LineSegment StartX=110.5 StartY=8 StartZ=0 EndX=80 EndY=8 EndZ=0
    g18: LineSegment StartX=80 StartY=8 StartZ=0 EndX=80 EndY=34 EndZ=0
    g19: GeomPoint X=95.25 Y=21 Z=0
    g20: LineSegment StartX=80 StartY=34 StartZ=0 EndX=110.5 EndY=8 EndZ=0
    g21: LineSegment StartX=110.5 StartY=34 StartZ=0 EndX=80 EndY=8 EndZ=0
    g22: LineSegment StartX=-110.5 StartY=34 StartZ=0 EndX=80 EndY=34 EndZ=0
    g23: Circle CenterX=-110.5 CenterY=-8 CenterZ=0 NormalX=0 NormalY=0 NormalZ=1 AngleXU=0 Radius=2.55
    g24: Circle CenterX=-110.5 CenterY=-34 CenterZ=0 NormalX=0 NormalY=0 NormalZ=1 AngleXU=0 Radius=2.55
    g25: Circle CenterX=-80 CenterY=-8 CenterZ=0 NormalX=0 NormalY=0 NormalZ=1 AngleXU=0 Radius=2.55
    g26: Circle CenterX=-80 CenterY=-34 CenterZ=0 NormalX=0 NormalY=0 NormalZ=1 AngleXU=0 Radius=2.55
    g27: LineSegment StartX=-110.5 StartY=-8 StartZ=0 EndX=-80 EndY=-8 EndZ=0
    g28: LineSegment StartX=-80 StartY=-8 StartZ=0 EndX=-80 EndY=-34 EndZ=0
    g29: LineSegment StartX=-80 StartY=-34 StartZ=0 EndX=-110.5 EndY=-34 EndZ=0
    g30: LineSegment StartX=-110.5 StartY=-34 StartZ=0 EndX=-110.5 EndY=-8 EndZ=0
    g31: GeomPoint X=-95.25 Y=-21 Z=0
    g32: LineSegment StartX=-110.5 StartY=-8 StartZ=0 EndX=-80 EndY=-34 EndZ=0
    g33: LineSegment StartX=-80 StartY=-8 StartZ=0 EndX=-110.5 EndY=-34 EndZ=0
    g34: LineSegment StartX=-110.5 StartY=34 StartZ=0 EndX=-110.5 EndY=-8 EndZ=0
    g35: Circle CenterX=80 CenterY=-8 CenterZ=0 NormalX=0 NormalY=0 NormalZ=1 AngleXU=0 Radius=2.55
    g36: Circle CenterX=80 CenterY=-34 CenterZ=0 NormalX=0 NormalY=0 NormalZ=1 AngleXU=0 Radius=2.55
    g37: Circle CenterX=110.5 CenterY=-8 CenterZ=0 NormalX=0 NormalY=0 NormalZ=1 AngleXU=0 Radius=2.55
    g38: Circle CenterX=110.5 CenterY=-34 CenterZ=0 NormalX=0 NormalY=0 NormalZ=1 AngleXU=0 Radius=2.55
    g39: LineSegment StartX=80 StartY=-8 StartZ=0 EndX=110.5 EndY=-8 EndZ=0
    g40: LineSegment StartX=110.5 StartY=-8 StartZ=0 EndX=110.5 EndY=-34 EndZ=0
    g41: LineSegment StartX=110.5 StartY=-34 StartZ=0 EndX=80 EndY=-34 EndZ=0
    g42: LineSegment StartX=80 StartY=-34 StartZ=0 EndX=80 EndY=-8 EndZ=0
    g43: GeomPoint X=95.25 Y=-21 Z=0
    g44: LineSegment StartX=80 StartY=-8 StartZ=0 EndX=110.5 EndY=-34 EndZ=0
    g45: LineSegment StartX=110.5 StartY=-8 StartZ=0 EndX=80 EndY=-34 EndZ=0
    g46: LineSegment StartX=-110.5 StartY=-8 StartZ=0 EndX=80 EndY=-8 EndZ=0
    g47: Circle CenterX=-10 CenterY=24 CenterZ=0 NormalX=0 NormalY=0 NormalZ=1 AngleXU=0 Radius=2.55
    g48: Circle CenterX=10 CenterY=24 CenterZ=0 NormalX=0 NormalY=0 NormalZ=1 AngleXU=0 Radius=2.55
    g49: Circle CenterX=10 CenterY=-24 CenterZ=0 NormalX=0 NormalY=0 NormalZ=1 AngleXU=0 Radius=2.55
    g50: Circle CenterX=-10 CenterY=-24 CenterZ=0 NormalX=0 NormalY=0 NormalZ=1 AngleXU=0 Radius=2.55
    g51: LineSegment StartX=-10 StartY=24 StartZ=0 EndX=10 EndY=24 EndZ=0
    g52: LineSegment StartX=10 StartY=24 StartZ=0 EndX=10 EndY=-24 EndZ=0
    g53: LineSegment StartX=10 StartY=-24 StartZ=0 EndX=-10 EndY=-24 EndZ=0
    g54: LineSegment StartX=-10 StartY=-24 StartZ=0 EndX=-10 EndY=24 EndZ=0
  constraints (130):
    c: Coincident(g4,g5)
    c: Coincident(g5,g6)
    c: Coincident(g6,g7)
    c: Coincident(g7,g4)
    c: Horizontal(g4)
    c: Horizontal(g6)
    c: Vertical(g5)
    c: Vertical(g7)
    c: Coincident(g4,g0)
    c: Coincident(g3,g5)
    c: Coincident(g2,g4)
    c: Coincident(g6,g1)
    c: Diameter(g0) = 5.1
    c: Equal(g0,g2)
    c: Equal(g2,g3)
    c: Equal(g3,g1)
    c: Coincident(g9,g0)
    c: Coincident(g9,g3)
    c: Coincident(g10,g2)
    c: Coincident(g10,g1)
    c: PointOnObject(g8,g10)
    c: PointOnObject(g8,g9)
    c: DistanceX(g6,g6) = 30.5
    c: DistanceY(g5,g5) = 26
    c: DistanceY(g-1,g8) = 21
    c: DistanceX(g8,g-1) = 95.25
    c: Coincident(g15,g16)
    c: Coincident(g16,g17)
    c: Coincident(g17,g18)
    c: Coincident(g18,g15)
    c: Horizontal(g15)
    c: Horizontal(g17)
    c: Vertical(g16)
    c: Vertical(g18)
    c: Coincident(g15,g11)
    c: Coincident(g14,g16)
    c: Coincident(g13,g15)
    c: Coincident(g17,g12)
    c: Diameter(g11) = 5.1
    c: Equal(g11,g13)
    c: Equal(g13,g14)
    c: Equal(g14,g12)
    c: Coincident(g20,g11)
    c: Coincident(g20,g14)
    c: Coincident(g21,g13)
    c: Coincident(g21,g12)
    c: PointOnObject(g19,g21)
    c: PointOnObject(g19,g20)
    c: DistanceX(g17,g17) = 30.5
    c: DistanceY(g16,g16) = 26
    c: Coincident(g0,g22)
    c: Coincident(g11,g22)
    c: Distance(g22) = 190.5
    c: Coincident(g27,g28)
    c: Coincident(g28,g29)
    c: Coincident(g29,g30)
    c: Coincident(g30,g27)
    c: Horizontal(g27)
    c: Horizontal(g29)
    c: Vertical(g28)
    c: Vertical(g30)
    c: Coincident(g27,g23)
    c: Coincident(g26,g28)
    c: Coincident(g25,g27)
    c: Coincident(g29,g24)
    c: Diameter(g23) = 5.1
    c: Equal(g23,g25)
    c: Equal(g25,g26)
    c: Equal(g26,g24)
    c: Coincident(g32,g23)
    c: Coincident(g32,g26)
    c: Coincident(g33,g25)
    c: Coincident(g33,g24)
    c: PointOnObject(g31,g33)
    c: PointOnObject(g31,g32)
    c: DistanceX(g29,g29) = 30.5
    c: DistanceY(g28,g28) = 26
    c: Coincident(g0,g34)
    c: Coincident(g23,g34)
    c: Distance(g34) = 42
    c: Perpendicular(g34,g22)
    c: Coincident(g39,g40)
    c: Coincident(g40,g41)
    c: Coincident(g41,g42)
    c: Coincident(g42,g39)
    c: Horizontal(g39)
    c: Horizontal(g41)
    c: Vertical(g40)
    c: Vertical(g42)
    c: Coincident(g39,g35)
    c: Coincident(g38,g40)
    c: Coincident(g37,g39)
    c: Coincident(g41,g36)
    c: Diameter(g35) = 5.1
    c: Equal(g35,g37)
    c: Equal(g37,g38)
    c: Equal(g38,g36)
    c: Coincident(g44,g35)
    c: Coincident(g44,g38)
    c: Coincident(g45,g37)
    c: Coincident(g45,g36)
    c: PointOnObject(g43,g45)
    c: PointOnObject(g43,g44)
    c: DistanceX(g41,g41) = 30.5
    c: DistanceY(g40,g40) = 26
    c: Coincident(g23,g46)
    c: Coincident(g35,g46)
    c: Equal(g22,g46)
    c: Parallel(g46,g22)
    c: Horizontal(g22)
    c: Coincident(g51,g52)
    c: Coincident(g52,g53)
    c: Coincident(g53,g54)
    c: Coincident(g54,g51)
    c: Horizontal(g51)
    c: Horizontal(g53)
    c: Vertical(g52)
    c: Vertical(g54)
    c: Coincident(g51,g47)
    c: Coincident(g52,g49)
    c: Diameter(g48) = 5.1
    c: Equal(g48,g47)
    c: Equal(g47,g50)
    c: Equal(g50,g49)
    c: Coincident(g48,g51)
    c: Coincident(g53,g50)
    c: DistanceX(g51,g51) = 20
    c: DistanceY(g52,g52) = 48
    c: DistanceY(g-1,g48) = 24
    c: DistanceX(g-1,g48) = 10
FEATURE [PartDesign::Hole] Hole
  AllowMultiFace = false
  BaseFeature = -> Pad011
  Depth = 25
  DepthType = 1
  Diameter = 5.1
  DrillPoint = 0
  DrillPointAngle = 118
  HoleCutCountersinkAngle = 90
  HoleCutDepth = 3
  HoleCutDiameter = 10
  HoleCutType = 1
  ModelActualThread = false
  Profile = -> Sketch024
  Tapered = false
  TaperedAngle = 90
  ThreadAngle = 0
  ThreadClass = 0
  ThreadCutOffInner = 0
  ThreadCutOffOuter = 0
  ThreadDirection = 0
  ThreadFit = 0
  ThreadPitch = 0
  ThreadSize = 0
  ThreadType = 0
  Threaded = false
FEATURE [Sketcher::SketchObject] Sketch025
  AttachmentOffset = pos=(0,0,6.35) rot=(0,0,1;0rad)
  MapMode = 5
  Placement = pos=(0,0,6.35) rot=(0,0,1;0rad)
  Support = -> [XY_Plane029]
  sketch-geometry (2):
    g0: Circle CenterX=-47 CenterY=0 CenterZ=0 NormalX=0 NormalY=0 NormalZ=1 AngleXU=0 Radius=12.5
    g1: Circle CenterX=47 CenterY=0 CenterZ=0 NormalX=0 NormalY=0 NormalZ=1 AngleXU=0 Radius=12.5
  constraints (5):
    c: Diameter(g0) = 25
    c: PointOnObject(g0,g-1)
    c: DistanceX(g0,g-1) = 47
    c: Symmetric(g0,g1,g-2)
    c: Equal(g0,g1)
FEATURE [PartDesign::Pocket] Pocket011
  AllowMultiFace = false
  BaseFeature = -> Hole
  Length = 5
  Length2 = 100
  Profile = -> Sketch025
  Type = 1
FEATURE [PartDesign::Body] Body010  label="Body"
  Group = -> [Sketch023,Pad011,Sketch024,Hole,Sketch025,Pocket011]
  Origin = -> Origin029
  Tip = -> Pocket011
FEATURE [PartDesign::CoordinateSystem] LCS_1
  AttacherType = Attacher::AttachEngine3D
  MapMode = 45
  Placement = pos=(1.15e-14,1.8e-15,0) rot=(0,0,1;0rad)
  Support = -> [Pocket011]
FEATURE [PartDesign::CoordinateSystem] LCS_2
  AttacherType = Attacher::AttachEngine3D
  MapMode = 45
  Placement = pos=(-95.25,-21,0) rot=(0,0,1;1.5708rad)
  Support = -> [Pocket011]
FEATURE [PartDesign::CoordinateSystem] LCS_3
  AttacherType = Attacher::AttachEngine3D
  MapMode = 45
  Placement = pos=(-95.25,21,0) rot=(0,0,1;1.5708rad)
  Support = -> [Pocket011]
FEATURE [PartDesign::CoordinateSystem] LCS_4
  AttacherType = Attacher::AttachEngine3D
  MapMode = 45
  Placement = pos=(95.25,-21,0) rot=(0,0,1;1.5708rad)
  Support = -> [Pocket011]
FEATURE [PartDesign::CoordinateSystem] LCS_5
  AttacherType = Attacher::AttachEngine3D
  MapMode = 45
  Placement = pos=(95.25,21,0) rot=(0,0,1;1.5708rad)
  Support = -> [Pocket011]
FEATURE [PartDesign::CoordinateSystem] LCS_6
  AttacherType = Attacher::AttachEngine3D
  MapMode = 45
  Placement = pos=(2.35e-14,0,6.35) rot=(0,0,1;0rad)
  Support = -> [Pocket011]
FEATURE [App::Part] Part017  label="bearing_plate"
  Group = -> [Body010,LCS_1,LCS_2,LCS_3,LCS_4,LCS_5,LCS_6]
  Origin = -> Origin024
